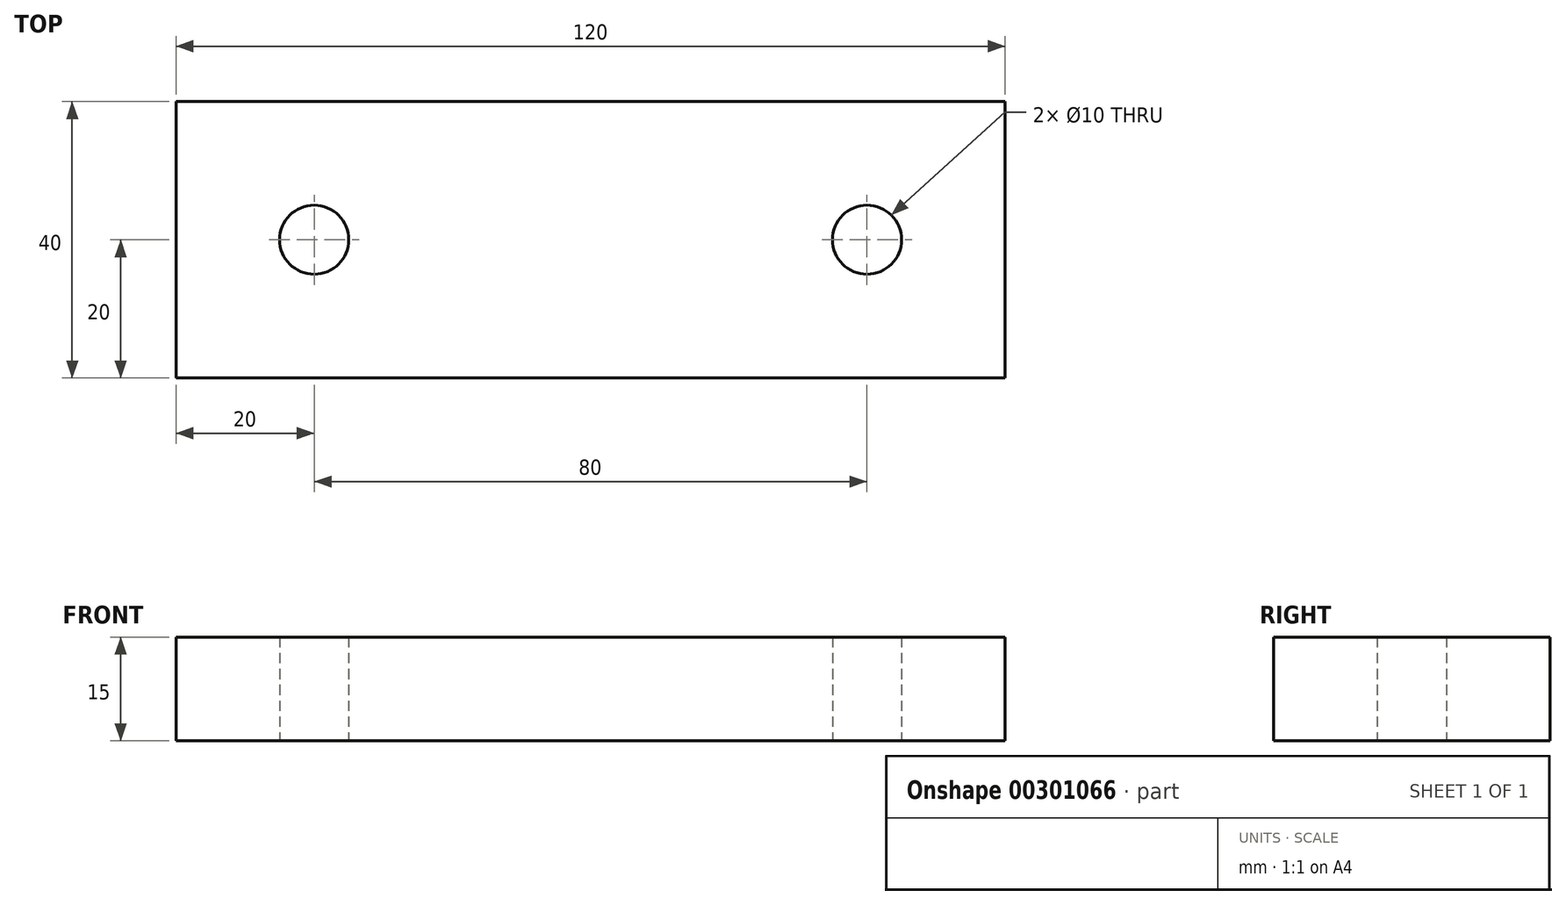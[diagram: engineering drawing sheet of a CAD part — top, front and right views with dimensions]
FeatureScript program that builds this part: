
annotation { "Feature Type Name" : "Feature", "Feature Type Description" : "" }
export const myFeature = defineFeature(function(context is Context, id is Id, definition is map)
    precondition{}
    {
        {
            var Q0;
            Q0=qCreatedBy(makeId("Top.planeOp"),FACE);
            var sketch = newSketch(context, id + "F0", { "sketchPlane" : qUnion([Q0])});
            skLineSegment(sketch, "E0.bottom", {"start": v(0, 0) * mm, "end": v(120, 0) * mm});
            skLineSegment(sketch, "E0.top", {"start": v(0, 40) * mm, "end": v(120, 40) * mm});
            skLineSegment(sketch, "E0.left", {"start": v(0, 0) * mm, "end": v(0, 40) * mm});
            skLineSegment(sketch, "E0.right", {"start": v(120, 0) * mm, "end": v(120, 40) * mm});
            skCircle(sketch, "E1", {"center": v(20, 20) * mm, "radius": 5 * mm});
            skCircle(sketch, "E2.1.0.0", {"center": v(100, 20) * mm, "radius": 5 * mm});
            skLineSegment(sketch, "E2.direction1", {"start": v(20, 20) * mm, "end": v(100, 20) * mm, "construction": true});
            skSolve(sketch);
        }
        {
            var Q0;
            Q0 = qSketchRegion(id + "F0", true);
            extrude(context, id + "F1", {"entities" : qUnion([Q0]), "depth" : 15 * mm});
        }
    });
